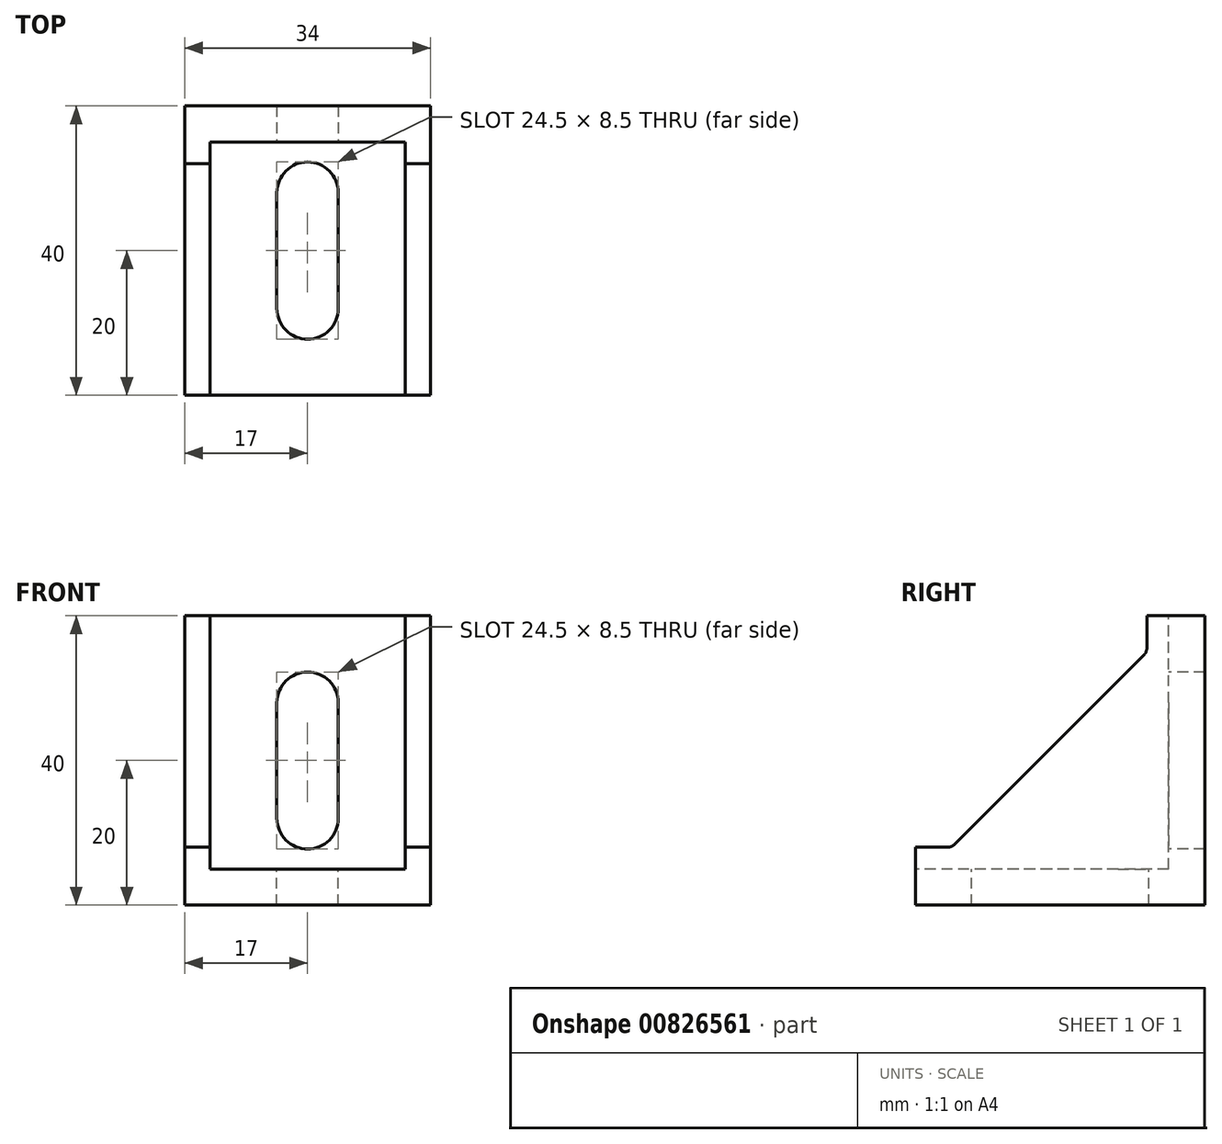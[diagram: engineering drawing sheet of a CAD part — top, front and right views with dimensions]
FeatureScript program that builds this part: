
annotation { "Feature Type Name" : "Feature", "Feature Type Description" : "" }
export const myFeature = defineFeature(function(context is Context, id is Id, definition is map)
    precondition{}
    {
        {
            var Q0;
            Q0=qCreatedBy(makeId("Top.planeOp"),FACE);
            var sketch = newSketch(context, id + "F0", { "sketchPlane" : qUnion([Q0])});
            skLineSegment(sketch, "E0.bottom", {"start": v(17, -20) * mm, "end": v(-17, -20) * mm});
            skLineSegment(sketch, "E0.top", {"start": v(17, 20) * mm, "end": v(-17, 20) * mm});
            skLineSegment(sketch, "E0.left", {"start": v(17, -20) * mm, "end": v(17, 20) * mm});
            skLineSegment(sketch, "E0.right", {"start": v(-17, -20) * mm, "end": v(-17, 20) * mm});
            skPoint(sketch, "E0.middle", {"position": v(0, 0) * mm});
            skSolve(sketch);
        }
        {
            var Q0;
            Q0 = qSketchRegion(id + "F0", true);
            extrude(context, id + "F1", {"entities" : qUnion([Q0]), "depth" : 40 * mm, "offsetDistance" : 25 * mm});
        }
        {
            var Q0;
            Q0=makeQuery(id+"F1.opExtrude","SWEPT_FACE",FACE,{"disambiguationData":[OSD([sQuery(id+"F0.wireOp",EDGE,"E0.bottom")])]});
            var sketch = newSketch(context, id + "F2", { "sketchPlane" : qUnion([Q0])});
            skPoint(sketch, "E1.middle", {"position": v(0, 20) * mm});
            skPoint(sketch, "E1.middle.positionSnap0", {"position": v(17, 20) * mm});
            skPoint(sketch, "E1.middle.positionSnap1", {"position": v(0, 0) * mm});
            skPoint(sketch, "E1.centerSnap0", {"position": v(17, 20) * mm});
            skPoint(sketch, "E1.centerSnap1", {"position": v(0, 0) * mm});
            skLineSegment(sketch, "E2", {"start": v(-17, 0) * mm, "end": v(-13.5, 0) * mm, "construction": true});
            skLineSegment(sketch, "E3", {"start": v(17, 0) * mm, "end": v(13.5, 0) * mm});
            skLineSegment(sketch, "E4", {"start": v(0, 0) * mm, "end": v(0, 5) * mm, "construction": true});
            skLineSegment(sketch, "E5", {"start": v(-13.5, 0) * mm, "end": v(-13.5, 5) * mm, "construction": true});
            skLineSegment(sketch, "E6", {"start": v(13.5, 0) * mm, "end": v(13.5, 5) * mm, "construction": true});
            skLineSegment(sketch, "E7.bottom", {"start": v(-13.5, 5) * mm, "end": v(13.5, 5) * mm});
            skLineSegment(sketch, "E7.top", {"start": v(-13.5, 40) * mm, "end": v(13.5, 40) * mm});
            skLineSegment(sketch, "E7.left", {"start": v(-13.5, 5) * mm, "end": v(-13.5, 40) * mm});
            skLineSegment(sketch, "E7.right", {"start": v(13.5, 5) * mm, "end": v(13.5, 40) * mm});
            skSolve(sketch);
        }
        {
            var Q0;
            Q0=makeQuery(id+"F2.imprint","IMPRINT",FACE,{"disambiguationData":[TD([[makeQuery(id+"F2.imprint","IMPRINT",EDGE,{"derivedFrom":sQuery(id+"F2.wireOp",EDGE,"E7.bottom")}),1.0]])]});
            extrude(context, id + "F3", {"entities" : qUnion([Q0]), "operationType" : NewBodyOperationType.REMOVE, "oppositeDirection" : true, "depth" : 35 * mm, "offsetDistance" : 25 * mm});
        }
        {
            var Q0;
            Q0=makeQuery(id+"F1.opExtrude","SWEPT_FACE",FACE,{"disambiguationData":[OSD([sQuery(id+"F0.wireOp",EDGE,"E0.right")])]});
            var sketch = newSketch(context, id + "F4", { "sketchPlane" : qUnion([Q0])});
            skLineSegment(sketch, "E8", {"start": v(-20, 40) * mm, "end": v(-12, 40) * mm, "construction": true});
            skLineSegment(sketch, "E9", {"start": v(-12, 40) * mm, "end": v(-12, 35) * mm, "construction": true});
            skLineSegment(sketch, "E10", {"start": v(20, 0) * mm, "end": v(20, 8) * mm, "construction": true});
            skLineSegment(sketch, "E11", {"start": v(20, 8) * mm, "end": v(15, 8) * mm, "construction": true});
            skLineSegment(sketch, "E12", {"start": v(-20, 40) * mm, "end": v(-12, 40) * mm});
            skLineSegment(sketch, "E13", {"start": v(20, 8) * mm, "end": v(20, 0) * mm});
            skLineSegment(sketch, "E14", {"start": v(-20, 0) * mm, "end": v(-20, 40) * mm});
            skLineSegment(sketch, "E15", {"start": v(-12, 35) * mm, "end": v(15, 8) * mm});
            skLineSegment(sketch, "E16", {"start": v(-12, 35) * mm, "end": v(-12, 40) * mm});
            skLineSegment(sketch, "E17", {"start": v(15, 8) * mm, "end": v(20, 8) * mm});
            skSolve(sketch);
        }
        {
            var Q0;
            Q0=makeQuery(id+"F4.imprint","IMPRINT",FACE,{"disambiguationData":[TD([[makeQuery(id+"F4.imprint","IMPRINT",EDGE,{"derivedFrom":sQuery(id+"F4.wireOp",EDGE,"E15")}),1.0]])]});
            extrude(context, id + "F5", {"entities" : qUnion([Q0]), "operationType" : NewBodyOperationType.REMOVE, "endBound" : BoundingType.THROUGH_ALL, "oppositeDirection" : true, "depth" : 25 * mm, "offsetDistance" : 25 * mm});
        }
        {
            var Q0;
            Q0=makeQuery(id+"F3.boolean.opBoolean","COPY",FACE,{"derivedFrom":makeQuery(id+"F3.opExtrude","SWEPT_FACE",FACE,{"disambiguationData":[OSD([sQuery(id+"F2.wireOp",EDGE,"E7.bottom")])]})});
            var sketch = newSketch(context, id + "F6", { "sketchPlane" : qUnion([Q0])});
            skLineSegment(sketch, "E18", {"start": v(0, 15) * mm, "end": v(0, 12.25) * mm, "construction": true});
            skLineSegment(sketch, "E19", {"start": v(-4.25, 12.25) * mm, "end": v(-4.25, -12.25) * mm, "construction": true});
            skLineSegment(sketch, "E20.bottom", {"start": v(-4.25, 12.25) * mm, "end": v(4.25, 12.25) * mm});
            skLineSegment(sketch, "E20.top", {"start": v(-4.25, -12.25) * mm, "end": v(4.25, -12.25) * mm});
            skLineSegment(sketch, "E20.left", {"start": v(-4.25, 12.25) * mm, "end": v(-4.25, -12.25) * mm});
            skLineSegment(sketch, "E20.right", {"start": v(4.25, 12.25) * mm, "end": v(4.25, -12.25) * mm});
            skLineSegment(sketch, "E21", {"start": v(0, 12.25) * mm, "end": v(0, 8) * mm, "construction": true});
            skCircle(sketch, "E22", {"center": v(0, 8) * mm, "radius": 4.25 * mm});
            skLineSegment(sketch, "E23", {"start": v(0, -12.25) * mm, "end": v(0, -8) * mm, "construction": true});
            skCircle(sketch, "E24", {"center": v(0, -8) * mm, "radius": 4.25 * mm});
            skSolve(sketch);
        }
        {
            var Q0;
            {var subQ0=sQuery(id+"F6.wireOp",EDGE,"E22");var subQ1=sQuery(id+"F6.wireOp",EDGE,"E20.left");var subQ2=makeQuery(id+"F6.imprint","INTERSECT",VERTEX,{"derivedFrom":[subQ1,subQ0]});Q0=makeQuery(id+"F6.imprint","IMPRINT",FACE,{"disambiguationData":[TD([[makeQuery(id+"F6.imprint","IMPRINT",EDGE,{"disambiguationData":[TD([[subQ2,-1.0]])],"derivedFrom":subQ1}),1.0]])]});}
            var Q1;
            {var subQ0=sQuery(id+"F6.wireOp",EDGE,"E22");var subQ1=makeQuery(id+"F6.imprint","INTERSECT",VERTEX,{"derivedFrom":[sQuery(id+"F6.wireOp",EDGE,"E20.bottom"),subQ0]});Q1=makeQuery(id+"F6.imprint","IMPRINT",FACE,{"disambiguationData":[TD([[makeQuery(id+"F6.imprint","IMPRINT",EDGE,{"disambiguationData":[TD([[subQ1,1.0]])],"derivedFrom":subQ0}),1.0]])]});}
            var Q2;
            {var subQ0=sQuery(id+"F6.wireOp",EDGE,"E24");var subQ1=makeQuery(id+"F6.imprint","INTERSECT",VERTEX,{"derivedFrom":[sQuery(id+"F6.wireOp",EDGE,"E20.left"),subQ0]});Q2=makeQuery(id+"F6.imprint","IMPRINT",FACE,{"disambiguationData":[TD([[makeQuery(id+"F6.imprint","IMPRINT",EDGE,{"disambiguationData":[TD([[subQ1,1.0]])],"derivedFrom":subQ0}),1.0]])]});}
            extrude(context, id + "F7", {"entities" : qUnion([Q0, Q1, Q2]), "operationType" : NewBodyOperationType.REMOVE, "endBound" : BoundingType.THROUGH_ALL, "oppositeDirection" : true, "depth" : 25 * mm, "offsetDistance" : 25 * mm});
        }
        {
            var Q0;
            Q0=makeQuery(id+"F3.boolean.opBoolean","COPY",FACE,{"derivedFrom":makeQuery(id+"F3.opExtrude","CAP_FACE",FACE,{"disambiguationData":[OSD([sQuery(id+"F2.wireOp",EDGE,"E7.bottom"),sQuery(id+"F2.wireOp",EDGE,"E7.top"),sQuery(id+"F2.wireOp",EDGE,"E7.left"),sQuery(id+"F2.wireOp",EDGE,"E7.right")])],"isStart":false})});
            var sketch = newSketch(context, id + "F8", { "sketchPlane" : qUnion([Q0])});
            skLineSegment(sketch, "E25", {"start": v(0, 5) * mm, "end": v(0, 7.75) * mm, "construction": true});
            skLineSegment(sketch, "E26", {"start": v(0, 7.75) * mm, "end": v(0, 32.25) * mm, "construction": true});
            skLineSegment(sketch, "E27", {"start": v(0, 7.75) * mm, "end": v(0, 12) * mm, "construction": true});
            skLineSegment(sketch, "E28", {"start": v(0, 32.25) * mm, "end": v(0, 28) * mm, "construction": true});
            skLineSegment(sketch, "E29", {"start": v(0, 7.75) * mm, "end": v(4.25, 7.75) * mm, "construction": true});
            skLineSegment(sketch, "E30", {"start": v(0, 32.25) * mm, "end": v(-4.25, 32.25) * mm, "construction": true});
            skLineSegment(sketch, "E31.bottom", {"start": v(-4.25, 32.25) * mm, "end": v(4.25, 32.25) * mm});
            skLineSegment(sketch, "E31.top", {"start": v(-4.25, 7.75) * mm, "end": v(4.25, 7.75) * mm});
            skLineSegment(sketch, "E31.left", {"start": v(-4.25, 32.25) * mm, "end": v(-4.25, 7.75) * mm});
            skLineSegment(sketch, "E31.right", {"start": v(4.25, 32.25) * mm, "end": v(4.25, 7.75) * mm});
            skCircle(sketch, "E32", {"center": v(0, 28) * mm, "radius": 4.25 * mm});
            skCircle(sketch, "E33", {"center": v(0, 12) * mm, "radius": 4.25 * mm});
            skSolve(sketch);
        }
        {
            var Q0;
            {var subQ0=sQuery(id+"F8.wireOp",EDGE,"E32");var subQ1=sQuery(id+"F8.wireOp",EDGE,"E31.left");var subQ2=makeQuery(id+"F8.imprint","INTERSECT",VERTEX,{"derivedFrom":[subQ1,subQ0]});Q0=makeQuery(id+"F8.imprint","IMPRINT",FACE,{"disambiguationData":[TD([[makeQuery(id+"F8.imprint","IMPRINT",EDGE,{"disambiguationData":[TD([[subQ2,-1.0]])],"derivedFrom":subQ1}),1.0]])]});}
            var Q1;
            {var subQ0=sQuery(id+"F8.wireOp",EDGE,"E32");var subQ1=makeQuery(id+"F8.imprint","INTERSECT",VERTEX,{"derivedFrom":[sQuery(id+"F8.wireOp",EDGE,"E31.bottom"),subQ0]});Q1=makeQuery(id+"F8.imprint","IMPRINT",FACE,{"disambiguationData":[TD([[makeQuery(id+"F8.imprint","IMPRINT",EDGE,{"disambiguationData":[TD([[subQ1,1.0]])],"derivedFrom":subQ0}),1.0]])]});}
            var Q2;
            {var subQ0=sQuery(id+"F8.wireOp",EDGE,"E33");var subQ1=makeQuery(id+"F8.imprint","INTERSECT",VERTEX,{"derivedFrom":[sQuery(id+"F8.wireOp",EDGE,"E31.left"),subQ0]});Q2=makeQuery(id+"F8.imprint","IMPRINT",FACE,{"disambiguationData":[TD([[makeQuery(id+"F8.imprint","IMPRINT",EDGE,{"disambiguationData":[TD([[subQ1,1.0]])],"derivedFrom":subQ0}),1.0]])]});}
            extrude(context, id + "F9", {"entities" : qUnion([Q0, Q1, Q2]), "operationType" : NewBodyOperationType.REMOVE, "endBound" : BoundingType.THROUGH_ALL, "oppositeDirection" : true, "depth" : 25 * mm, "offsetDistance" : 25 * mm});
        }
        {
            var Q0;
            {var subQ0=sQuery(id+"F4.wireOp",EDGE,"E17");var subQ1=sQuery(id+"F4.wireOp",EDGE,"E15");Q0=makeQuery(id+"F5.boolean.opBoolean","COPY",EDGE,{"disambiguationData":[TD([makeQuery(id+"F1.opExtrude","SWEPT_FACE",FACE,{"disambiguationData":[OSD([sQuery(id+"F0.wireOp",EDGE,"E0.right")])]})])],"derivedFrom":makeQuery(id+"F5.opExtrude","SWEPT_EDGE",EDGE,{"disambiguationData":[OSD([subQ1,subQ0])]})});}
            var Q1;
            {var subQ0=sQuery(id+"F4.wireOp",EDGE,"E15");var subQ1=sQuery(id+"F4.wireOp",EDGE,"E17");Q1=makeQuery(id+"F5.boolean.opBoolean","COPY",EDGE,{"disambiguationData":[TD([makeQuery(id+"F1.opExtrude","SWEPT_FACE",FACE,{"disambiguationData":[OSD([sQuery(id+"F0.wireOp",EDGE,"E0.left")])]})])],"derivedFrom":makeQuery(id+"F5.opExtrude","SWEPT_EDGE",EDGE,{"disambiguationData":[OSD([subQ0,subQ1])]})});}
            var Q2;
            {var subQ0=sQuery(id+"F0.wireOp",EDGE,"E0.bottom");var subQ1=sQuery(id+"F4.wireOp",EDGE,"E17");Q2=makeQuery(id+"F5.boolean.opBoolean","COPY",EDGE,{"disambiguationData":[TD([makeQuery(id+"F1.opExtrude","SWEPT_FACE",FACE,{"disambiguationData":[OSD([sQuery(id+"F0.wireOp",EDGE,"E0.left")])]})])],"derivedFrom":makeQuery(id+"F5.opExtrude","SWEPT_EDGE",EDGE,{"disambiguationData":[OSD([subQ0,sQuery(id+"F0.wireOp",EDGE,"E0.right"),sQuery(id+"F4.wireOp",EDGE,"E13"),subQ1])]})});}
            var Q3;
            {var subQ0=sQuery(id+"F0.wireOp",EDGE,"E0.bottom");var subQ1=sQuery(id+"F0.wireOp",EDGE,"E0.right");var subQ2=sQuery(id+"F4.wireOp",EDGE,"E17");Q3=makeQuery(id+"F5.boolean.opBoolean","COPY",EDGE,{"disambiguationData":[TD([makeQuery(id+"F1.opExtrude","SWEPT_FACE",FACE,{"disambiguationData":[OSD([subQ1])]})])],"derivedFrom":makeQuery(id+"F5.opExtrude","SWEPT_EDGE",EDGE,{"disambiguationData":[OSD([subQ0,subQ1,sQuery(id+"F4.wireOp",EDGE,"E13"),subQ2])]})});}
            var Q4;
            {var subQ0=sQuery(id+"F4.wireOp",EDGE,"E15");var subQ1=sQuery(id+"F4.wireOp",EDGE,"E16");Q4=makeQuery(id+"F5.boolean.opBoolean","COPY",EDGE,{"disambiguationData":[TD([makeQuery(id+"F1.opExtrude","SWEPT_FACE",FACE,{"disambiguationData":[OSD([sQuery(id+"F0.wireOp",EDGE,"E0.left")])]})])],"derivedFrom":makeQuery(id+"F5.opExtrude","SWEPT_EDGE",EDGE,{"disambiguationData":[OSD([subQ0,subQ1])]})});}
            var Q5;
            {var subQ0=sQuery(id+"F4.wireOp",EDGE,"E16");var subQ1=sQuery(id+"F4.wireOp",EDGE,"E15");Q5=makeQuery(id+"F5.boolean.opBoolean","COPY",EDGE,{"disambiguationData":[TD([makeQuery(id+"F1.opExtrude","SWEPT_FACE",FACE,{"disambiguationData":[OSD([sQuery(id+"F0.wireOp",EDGE,"E0.right")])]})])],"derivedFrom":makeQuery(id+"F5.opExtrude","SWEPT_EDGE",EDGE,{"disambiguationData":[OSD([subQ1,subQ0])]})});}
            var Q6;
            {var subQ0=sQuery(id+"F0.wireOp",EDGE,"E0.right");var subQ1=sQuery(id+"F4.wireOp",EDGE,"E16");Q6=makeQuery(id+"F5.boolean.opBoolean","COPY",EDGE,{"disambiguationData":[TD([makeQuery(id+"F1.opExtrude","SWEPT_FACE",FACE,{"disambiguationData":[OSD([subQ0])]})])],"derivedFrom":makeQuery(id+"F5.opExtrude","SWEPT_EDGE",EDGE,{"disambiguationData":[OSD([subQ0,sQuery(id+"F4.wireOp",EDGE,"E12"),subQ1])]})});}
            var Q7;
            {var subQ0=sQuery(id+"F0.wireOp",EDGE,"E0.right");var subQ1=sQuery(id+"F0.wireOp",EDGE,"E0.left");var subQ2=sQuery(id+"F4.wireOp",EDGE,"E16");Q7=makeQuery(id+"F5.boolean.opBoolean","COPY",EDGE,{"disambiguationData":[TD([makeQuery(id+"F1.opExtrude","SWEPT_FACE",FACE,{"disambiguationData":[OSD([subQ1])]})])],"derivedFrom":makeQuery(id+"F5.opExtrude","SWEPT_EDGE",EDGE,{"disambiguationData":[OSD([subQ0,sQuery(id+"F4.wireOp",EDGE,"E12"),subQ2])]})});}
            fillet(context, id + "F10", {"entities" : qUnion([Q0, Q1, Q2, Q3, Q4, Q5, Q6, Q7]), "radius" : 1.5 * mm, "tangentPropagation" : true, "allowEdgeOverflow" : false});
        }
    });
